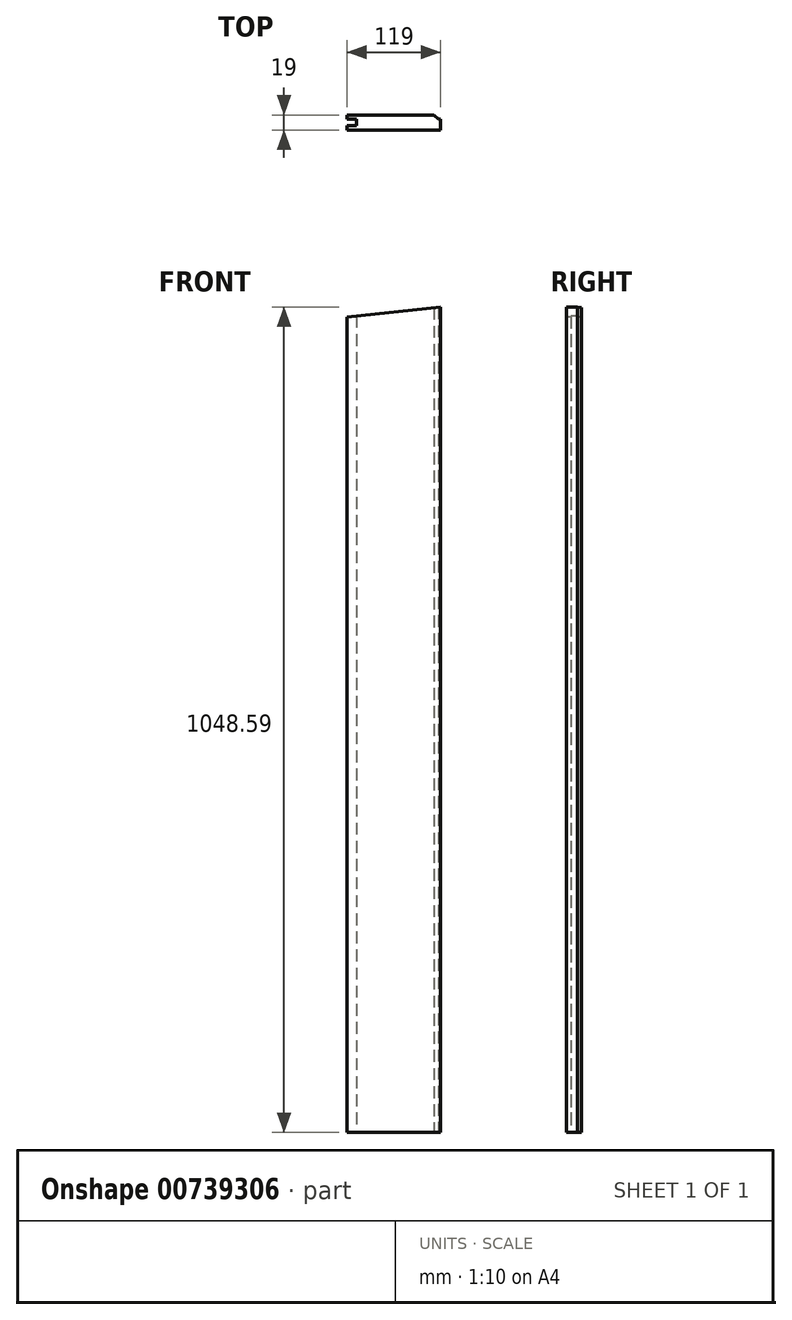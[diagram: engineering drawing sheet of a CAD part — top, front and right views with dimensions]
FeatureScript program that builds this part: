
annotation { "Feature Type Name" : "Feature", "Feature Type Description" : "" }
export const myFeature = defineFeature(function(context is Context, id is Id, definition is map)
    precondition{}
    {
        {
            var Q0;
            Q0=qCreatedBy(makeId("Top.planeOp"),FACE);
            var sketch = newSketch(context, id + "F0", { "sketchPlane" : qUnion([Q0])});
            skLineSegment(sketch, "E0.bottom", {"start": v(0, -9.5) * mm, "end": v(136, -9.5) * mm});
            skLineSegment(sketch, "E0.top", {"start": v(0, 9.5) * mm, "end": v(110.5, 9.5) * mm});
            skLineSegment(sketch, "E0.left", {"start": v(0, -9.5) * mm, "end": v(0, -4) * mm});
            skLineSegment(sketch, "E0.right", {"start": v(136, -9.5) * mm, "end": v(136, -4) * mm});
            skLineSegment(sketch, "E1", {"start": v(0, -4) * mm, "end": v(12, -4) * mm});
            skLineSegment(sketch, "E2", {"start": v(12, -4) * mm, "end": v(12, 4) * mm});
            skLineSegment(sketch, "E3", {"start": v(12, 4) * mm, "end": v(0, 4) * mm});
            skLineSegment(sketch, "E4.trimOffspring", {"start": v(0, 4) * mm, "end": v(0, 9.5) * mm});
            skLineSegment(sketch, "E5", {"start": v(136, -4) * mm, "end": v(146, -4) * mm});
            skLineSegment(sketch, "E6", {"start": v(146, -4) * mm, "end": v(146, 4) * mm});
            skLineSegment(sketch, "E7", {"start": v(146, 4) * mm, "end": v(116, 4) * mm});
            skLineSegment(sketch, "E8.trimOffspring", {"start": v(116, 4) * mm, "end": v(110.5, 9.5) * mm});
            skSolve(sketch);
        }
        {
            var Q0;
            Q0=makeQuery(id+"F0.imprint","IMPRINT",FACE,{"disambiguationData":[TD([[makeQuery(id+"F0.imprint","IMPRINT",EDGE,{"derivedFrom":sQuery(id+"F0.wireOp",EDGE,"E0.bottom")}),1.0]])]});
            extrude(context, id + "F1", {"entities" : qUnion([Q0]), "depth" : 1100 * mm, "offsetDistance" : 25 * mm});
        }
        {
            var Q0;
            Q0=makeQuery(id+"F1.opExtrude","SWEPT_FACE",FACE,{"disambiguationData":[OSD([sQuery(id+"F0.wireOp",EDGE,"E0.top")])]});
            var sketch = newSketch(context, id + "F2", { "sketchPlane" : qUnion([Q0])});
            skLineSegment(sketch, "E9", {"start": v(-608.15, 1100) * mm, "end": v(819, 950) * mm});
            skLineSegment(sketch, "E10", {"start": v(819, 950) * mm, "end": v(819, 1100) * mm});
            skLineSegment(sketch, "E11", {"start": v(819, 1100) * mm, "end": v(-608.15, 1100) * mm});
            skSolve(sketch);
        }
        {
            var Q0;
            {var subQ0=sQuery(id+"F2.wireOp",EDGE,"E11");var subQ1=sQuery(id+"F2.wireOp",EDGE,"E9");var subQ2=makeQuery(id+"F2.imprint","INTERSECT",VERTEX,{"derivedFrom":[subQ1,subQ0]});Q0=makeQuery(id+"F2.imprint","IMPRINT",FACE,{"disambiguationData":[TD([[makeQuery(id+"F2.imprint","IMPRINT",EDGE,{"disambiguationData":[TD([[subQ2,-1.0]])],"derivedFrom":subQ1}),1.0]])]});}
            var Q1;
            {var subQ0=sQuery(id+"F2.wireOp",EDGE,"E10");Q1=makeQuery(id+"F2.imprint","IMPRINT",FACE,{"disambiguationData":[TD([[makeQuery(id+"F2.imprint","IMPRINT",EDGE,{"derivedFrom":subQ0}),1.0]])]});}
            var Q2;
            {var subQ0=sQuery(id+"F2.wireOp",EDGE,"E9");var subQ1=sQuery(id+"F0.wireOp",EDGE,"E0.top");var subQ2=makeQuery(id+"F1.opExtrude","SWEPT_EDGE",EDGE,{"disambiguationData":[OSD([subQ1,sQuery(id+"F0.wireOp",EDGE,"E8.trimOffspring")])]});var subQ3=makeQuery(id+"F2.imprint","INTERSECT",VERTEX,{"derivedFrom":[subQ2,subQ0]});Q2=makeQuery(id+"F2.imprint","IMPRINT",FACE,{"disambiguationData":[TD([[makeQuery(id+"F2.imprint","IMPRINT",EDGE,{"disambiguationData":[TD([[subQ3,-1.0]])],"derivedFrom":subQ0}),1.0]])]});}
            extrude(context, id + "F3", {"entities" : qUnion([Q0, Q1, Q2]), "operationType" : NewBodyOperationType.REMOVE, "endBound" : BoundingType.THROUGH_ALL, "oppositeDirection" : true, "depth" : 25 * mm, "offsetDistance" : 25 * mm});
        }
        {
            var Q0;
            Q0=makeQuery(id+"F1.opExtrude","CAP_FACE",FACE,{"disambiguationData":[OSD([sQuery(id+"F0.wireOp",EDGE,"E0.bottom"),sQuery(id+"F0.wireOp",EDGE,"E0.top"),sQuery(id+"F0.wireOp",EDGE,"E0.left"),sQuery(id+"F0.wireOp",EDGE,"E0.right"),sQuery(id+"F0.wireOp",EDGE,"E1"),sQuery(id+"F0.wireOp",EDGE,"E2"),sQuery(id+"F0.wireOp",EDGE,"E3"),sQuery(id+"F0.wireOp",EDGE,"E4.trimOffspring"),sQuery(id+"F0.wireOp",EDGE,"E5"),sQuery(id+"F0.wireOp",EDGE,"E6"),sQuery(id+"F0.wireOp",EDGE,"E7"),sQuery(id+"F0.wireOp",EDGE,"E8.trimOffspring")])],"isStart":true});
            var sketch = newSketch(context, id + "F4", { "sketchPlane" : qUnion([Q0])});
            skLineSegment(sketch, "E12.bottom", {"start": v(119, 9.5) * mm, "end": v(146, 9.5) * mm});
            skLineSegment(sketch, "E12.top", {"start": v(119, -9.5) * mm, "end": v(146, -9.5) * mm});
            skLineSegment(sketch, "E12.left", {"start": v(119, 9.5) * mm, "end": v(119, -9.5) * mm});
            skLineSegment(sketch, "E12.right", {"start": v(146, 9.5) * mm, "end": v(146, -9.5) * mm});
            skSolve(sketch);
        }
        {
            var Q0;
            {var subQ0=sQuery(id+"F4.wireOp",EDGE,"E12.top");Q0=makeQuery(id+"F4.imprint","IMPRINT",FACE,{"disambiguationData":[TD([[makeQuery(id+"F4.imprint","IMPRINT",EDGE,{"derivedFrom":subQ0}),1.0]])]});}
            var Q1;
            {var subQ5=makeQuery(id+"F1.opExtrude","CAP_EDGE",EDGE,{"disambiguationData":[OSD([sQuery(id+"F0.wireOp",EDGE,"E0.right")])],"isStart":true});Q1=makeQuery(id+"F4.imprint","IMPRINT",FACE,{"disambiguationData":[TD([[makeQuery(id+"F4.imprint","IMPRINT",EDGE,{"derivedFrom":subQ5}),-1.0]])]});}
            var Q2;
            {var subQ1=makeQuery(id+"F1.opExtrude","CAP_EDGE",EDGE,{"disambiguationData":[OSD([sQuery(id+"F0.wireOp",EDGE,"E0.right")])],"isStart":true});Q2=makeQuery(id+"F4.imprint","IMPRINT",FACE,{"disambiguationData":[TD([[makeQuery(id+"F4.imprint","IMPRINT",EDGE,{"derivedFrom":subQ1}),1.0]])]});}
            extrude(context, id + "F5", {"entities" : qUnion([Q0, Q1, Q2]), "operationType" : NewBodyOperationType.REMOVE, "endBound" : BoundingType.THROUGH_ALL, "oppositeDirection" : true, "depth" : 25 * mm, "offsetDistance" : 25 * mm});
        }
    });
